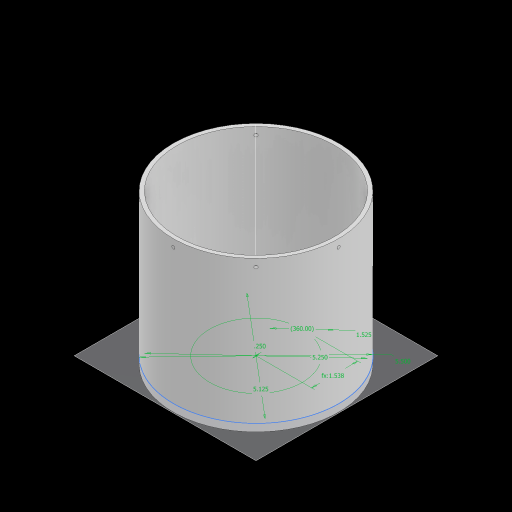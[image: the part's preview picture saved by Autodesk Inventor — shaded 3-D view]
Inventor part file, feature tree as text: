
AUTODESK INVENTOR PART (.ipt)
format: ipt  version: 2023 (Build 270158000, 158)  size: 163,840 bytes
history: native  units: in
note: dims shown in document units (in); Inventor stores cm internally (conversion verified against a paired STEP export)
features: extrude x5, sketch x3, pattern_circular x3, plane x1
ambient origin geometry x8: Origin, YZ Plane, XZ Plane, XY Plane, X Axis, Y Axis, Z Axis, Center Point
bodies: Solid1 (feature_tree)
feature tree (12):
  sketch  "Sketch1"  dims[d0=5.25in]
  extrude  "Extrusion1"  Depth=0.25in
  extrude  "Extrusion2"  Depth=0.25in TaperAngle=0.0deg
  plane  "Work Plane1"
  sketch  "Sketch2"  dims[d2=1.5748in d3=5.125in d4=1.525in d5=1.5375in d6=360.0deg d7=0.25in d8=5.5in]
  extrude  "Extrusion3"  Depth=0.25in
  pattern_circular  "Circular Pattern1"  [2 undecoded]
  extrude  "Extrusion4"  Depth=0.25in
  pattern_circular  "Circular Pattern2"  [2 undecoded]
  extrude  "Extrusion5"  Depth=0.25in TaperAngle=360.0deg
  pattern_circular  "Circular Pattern3"  [2 undecoded]
  sketch  "Sketch3"  dims[d9=4.75in d10=0.0in d11=0.25in d12=0.0in d13=2.75in d14=0.1in d15=0.25in d16=0.1in d17=0.0in d18=3.1496in d19=360.0deg d21=1.0in d22=0.0in d23=1.5748in d24=360.0deg d26=0.1in d27=1.5in d28=4.75in d29=0.0in d30=1.5748in d31=360.0deg]
note: 6 required parameter values undecoded (feature->parameter linkage not recoverable at this tier; creation-order binding heuristic only, values carry confidence <= 0.55)
